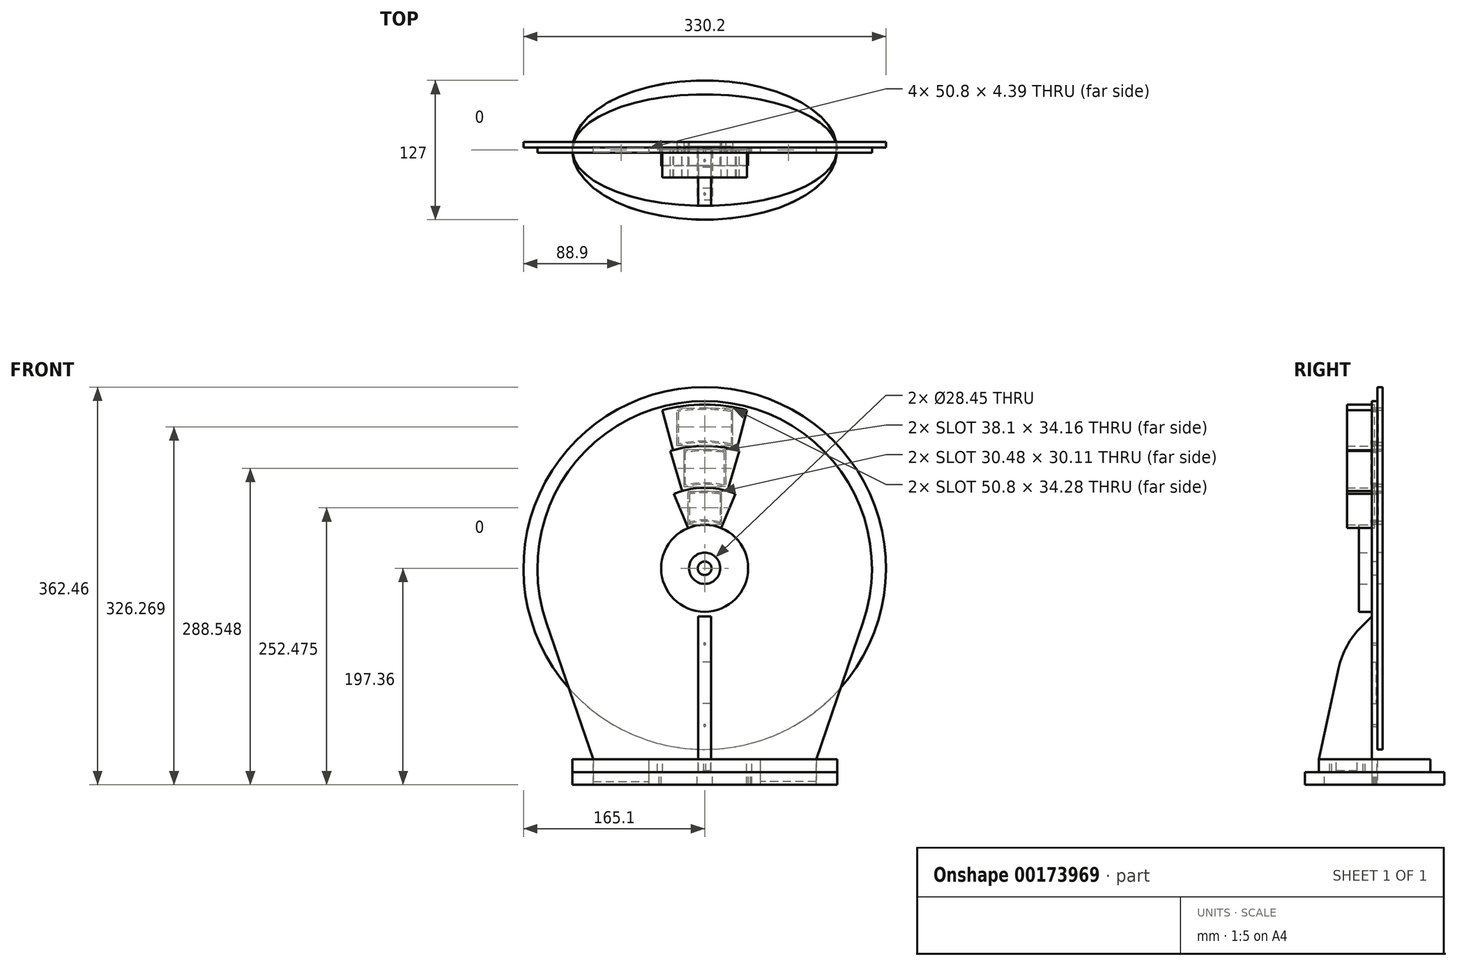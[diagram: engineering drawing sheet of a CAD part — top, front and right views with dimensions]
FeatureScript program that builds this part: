
annotation { "Feature Type Name" : "Feature", "Feature Type Description" : "" }
export const myFeature = defineFeature(function(context is Context, id is Id, definition is map)
    precondition{}
    {
        {
            var Q0;
            Q0=qCreatedBy(makeId("Front.planeOp"),FACE);
            var sketch = newSketch(context, id + "F0", { "sketchPlane" : qUnion([Q0])});
            skArc(sketch, "E0", {"start": v(144.21, 147.57) * mm, "mid": v(0, 349.25) * mm, "end": v(-144.21, 147.57) * mm});
            skLineSegment(sketch, "E1", {"start": v(0, 0) * mm, "end": v(0, 196.85) * mm, "construction": true});
            skLineSegment(sketch, "E2", {"start": v(-101.6, 22.86) * mm, "end": v(0, 22.86) * mm, "construction": true});
            skLineSegment(sketch, "E3", {"start": v(-101.6, 22.86) * mm, "end": v(-144.21, 147.57) * mm});
            skLineSegment(sketch, "E4.MirrorCS", {"start": v(101.6, 22.86) * mm, "end": v(0, 22.86) * mm, "construction": true});
            skLineSegment(sketch, "E5.MirrorCS", {"start": v(101.6, 22.86) * mm, "end": v(144.21, 147.57) * mm});
            skLineSegment(sketch, "E6", {"start": v(-101.6, 22.86) * mm, "end": v(-101.6, 2.54) * mm});
            skLineSegment(sketch, "E7", {"start": v(-101.6, 2.54) * mm, "end": v(-50.8, 2.54) * mm});
            skLineSegment(sketch, "E8", {"start": v(-50.8, 2.54) * mm, "end": v(-50.8, 22.86) * mm});
            skLineSegment(sketch, "E9", {"start": v(-50.8, 22.86) * mm, "end": v(0, 22.86) * mm});
            skLineSegment(sketch, "E10.MirrorCS", {"start": v(50.8, 2.54) * mm, "end": v(50.8, 22.86) * mm});
            skLineSegment(sketch, "E11.MirrorCS", {"start": v(50.8, 22.86) * mm, "end": v(0, 22.86) * mm});
            skLineSegment(sketch, "E12.MirrorCS", {"start": v(101.6, 22.86) * mm, "end": v(101.6, 2.54) * mm});
            skLineSegment(sketch, "E13.MirrorCS", {"start": v(101.6, 2.54) * mm, "end": v(50.8, 2.54) * mm});
            skCircle(sketch, "E14", {"center": v(0, 196.85) * mm, "radius": 6.22 * mm});
            skCircle(sketch, "E15", {"center": v(0, 196.85) * mm, "radius": 165.1 * mm, "construction": true});
            skCircle(sketch, "E16", {"center": v(0, 196.85) * mm, "radius": 39.69 * mm, "construction": true});
            skLineSegment(sketch, "E17.bottom", {"start": v(5.71, 73.66) * mm, "end": v(-5.72, 73.66) * mm});
            skLineSegment(sketch, "E17.top", {"start": v(5.71, 111.5) * mm, "end": v(-5.72, 111.5) * mm});
            skLineSegment(sketch, "E17.left", {"start": v(5.71, 73.66) * mm, "end": v(5.71, 111.5) * mm});
            skLineSegment(sketch, "E17.right", {"start": v(-5.72, 73.66) * mm, "end": v(-5.72, 111.5) * mm});
            skPoint(sketch, "E17.middle", {"position": v(0, 92.58) * mm});
            skCircle(sketch, "E18", {"center": v(0, 53.66) * mm, "radius": 0.95 * mm});
            skCircle(sketch, "E19", {"center": v(0, 128.02) * mm, "radius": 0.95 * mm});
            skSolve(sketch);
        }
        {
            var Q0;
            Q0=makeQuery(id+"F0.imprint","IMPRINT",FACE,{"disambiguationData":[TD([[makeQuery(id+"F0.imprint","IMPRINT",EDGE,{"derivedFrom":sQuery(id+"F0.wireOp",EDGE,"E0")}),1.0]])]});
            extrude(context, id + "F1", {"entities" : qUnion([Q0]), "endBound" : BoundingType.SYMMETRIC, "depth" : 4.9 * mm});
        }
        {
            var Q0;
            Q0=makeQuery(id+"F1.opExtrude","CAP_FACE",FACE,{"disambiguationData":[OSD([sQuery(id+"F0.wireOp",EDGE,"E0"),sQuery(id+"F0.wireOp",EDGE,"E3"),sQuery(id+"F0.wireOp",EDGE,"E5.MirrorCS"),sQuery(id+"F0.wireOp",EDGE,"E6"),sQuery(id+"F0.wireOp",EDGE,"E7"),sQuery(id+"F0.wireOp",EDGE,"E8"),sQuery(id+"F0.wireOp",EDGE,"E9"),sQuery(id+"F0.wireOp",EDGE,"E10.MirrorCS"),sQuery(id+"F0.wireOp",EDGE,"E11.MirrorCS"),sQuery(id+"F0.wireOp",EDGE,"E12.MirrorCS"),sQuery(id+"F0.wireOp",EDGE,"E13.MirrorCS"),sQuery(id+"F0.wireOp",EDGE,"E14")])],"isStart":false});
            var sketch = newSketch(context, id + "F2", { "sketchPlane" : qUnion([Q0])});
            skCircle(sketch, "E20", {"center": v(0, 196.85) * mm, "radius": 14.22 * mm});
            skCircle(sketch, "E21", {"center": v(0, 196.85) * mm, "radius": 39.62 * mm});
            skSolve(sketch);
        }
        {
            var Q0;
            Q0 = qSketchRegion(id + "F2", true);
            extrude(context, id + "F3", {"entities" : qUnion([Q0]), "depth" : 11.68 * mm});
        }
        {
            var Q0;
            Q0=makeQuery(id+"F1.opExtrude","CAP_FACE",FACE,{"disambiguationData":[OSD([sQuery(id+"F0.wireOp",EDGE,"E0"),sQuery(id+"F0.wireOp",EDGE,"E3"),sQuery(id+"F0.wireOp",EDGE,"E5.MirrorCS"),sQuery(id+"F0.wireOp",EDGE,"E6"),sQuery(id+"F0.wireOp",EDGE,"E7"),sQuery(id+"F0.wireOp",EDGE,"E8"),sQuery(id+"F0.wireOp",EDGE,"E9"),sQuery(id+"F0.wireOp",EDGE,"E10.MirrorCS"),sQuery(id+"F0.wireOp",EDGE,"E11.MirrorCS"),sQuery(id+"F0.wireOp",EDGE,"E12.MirrorCS"),sQuery(id+"F0.wireOp",EDGE,"E13.MirrorCS"),sQuery(id+"F0.wireOp",EDGE,"E14")])],"isStart":true});
            var sketch = newSketch(context, id + "F4", { "sketchPlane" : qUnion([Q0])});
            skCircle(sketch, "E22", {"center": v(0, 196.85) * mm, "radius": 14.22 * mm});
            skCircle(sketch, "E23", {"center": v(0, 196.85) * mm, "radius": 165.1 * mm});
            skSolve(sketch);
        }
        {
            var Q0;
            Q0=makeQuery(id+"F4.imprint","IMPRINT",FACE,{"disambiguationData":[TD([[makeQuery(id+"F4.imprint","IMPRINT",EDGE,{"derivedFrom":sQuery(id+"F4.wireOp",EDGE,"E22")}),-1.0]])]});
            var Q1;
            Q1=makeQuery(id+"F4.imprint","IMPRINT",FACE,{"disambiguationData":[TD([[makeQuery(id+"F4.imprint","IMPRINT",EDGE,{"derivedFrom":makeQuery(id+"F1.opExtrude","CAP_EDGE",EDGE,{"disambiguationData":[OSD([sQuery(id+"F0.wireOp",EDGE,"E17.bottom")])],"isStart":true})}),1.0]])]});
            var Q2;
            {var subQ5=makeQuery(id+"F1.opExtrude","CAP_EDGE",EDGE,{"disambiguationData":[OSD([sQuery(id+"F0.wireOp",EDGE,"E0")])],"isStart":true});Q2=makeQuery(id+"F4.imprint","IMPRINT",FACE,{"disambiguationData":[TD([[makeQuery(id+"F4.imprint","IMPRINT",EDGE,{"derivedFrom":subQ5}),1.0]])]});}
            var Q3;
            Q3=makeQuery(id+"F4.imprint","IMPRINT",FACE,{"disambiguationData":[TD([[makeQuery(id+"F4.imprint","IMPRINT",EDGE,{"derivedFrom":makeQuery(id+"F1.opExtrude","CAP_EDGE",EDGE,{"disambiguationData":[OSD([sQuery(id+"F0.wireOp",EDGE,"E19")])],"isStart":true})}),-1.0]])]});
            var Q4;
            Q4=makeQuery(id+"F4.imprint","IMPRINT",FACE,{"disambiguationData":[TD([[makeQuery(id+"F4.imprint","IMPRINT",EDGE,{"derivedFrom":makeQuery(id+"F1.opExtrude","CAP_EDGE",EDGE,{"disambiguationData":[OSD([sQuery(id+"F0.wireOp",EDGE,"E18")])],"isStart":true})}),-1.0]])]});
            extrude(context, id + "F5", {"entities" : qUnion([Q0, Q1, Q2, Q3, Q4]), "depth" : 4.9 * mm});
        }
        {
            var Q0;
            Q0=qCreatedBy(makeId("Front.planeOp"),FACE);
            var sketch = newSketch(context, id + "F6", { "sketchPlane" : qUnion([Q0])});
            skArc(sketch, "E24.0.1", {"start": v(144.21, 147.57) * mm, "mid": v(0, 349.25) * mm, "end": v(-144.21, 147.57) * mm, "construction": true});
            skCircle(sketch, "E25.0", {"center": v(0, 196.85) * mm, "radius": 165.1 * mm, "construction": true});
            skCircle(sketch, "E26.0", {"center": v(0, 196.85) * mm, "radius": 39.69 * mm, "construction": true});
            skCircle(sketch, "E27", {"center": v(0, 196.85) * mm, "radius": 152.4 * mm, "construction": true});
            skCircle(sketch, "E28", {"center": v(0, 196.85) * mm, "radius": 146.05 * mm});
            skCircle(sketch, "E29", {"center": v(0, 196.85) * mm, "radius": 114.62 * mm});
            skCircle(sketch, "E30", {"center": v(0, 196.85) * mm, "radius": 108.27 * mm});
            skCircle(sketch, "E31", {"center": v(0, 196.85) * mm, "radius": 76.52 * mm});
            skCircle(sketch, "E32", {"center": v(0, 196.85) * mm, "radius": 70.17 * mm});
            skCircle(sketch, "E33", {"center": v(0, 196.85) * mm, "radius": 42.86 * mm});
            skLineSegment(sketch, "E34", {"start": v(0, 196.85) * mm, "end": v(0, 267.02) * mm, "construction": true});
            skLineSegment(sketch, "E35", {"start": v(-15.24, 265.34) * mm, "end": v(-15.24, 236.91) * mm});
            skLineSegment(sketch, "E36.MirrorCS", {"start": v(15.24, 265.34) * mm, "end": v(15.24, 236.91) * mm});
            skLineSegment(sketch, "E37", {"start": v(-19.05, 270.96) * mm, "end": v(-19.05, 303.43) * mm});
            skLineSegment(sketch, "E38.MirrorCS", {"start": v(19.05, 270.96) * mm, "end": v(19.05, 303.43) * mm});
            skLineSegment(sketch, "E39", {"start": v(-25.4, 340.67) * mm, "end": v(-25.4, 308.62) * mm});
            skLineSegment(sketch, "E40.MirrorCS", {"start": v(25.4, 340.67) * mm, "end": v(25.4, 308.62) * mm});
            skSolve(sketch);
        }
        {
            var Q0;
            {var subQ0=sQuery(id+"F6.wireOp",EDGE,"E39");Q0=makeQuery(id+"F6.imprint","IMPRINT",FACE,{"disambiguationData":[TD([[makeQuery(id+"F6.imprint","IMPRINT",EDGE,{"derivedFrom":subQ0}),1.0]])]});}
            var Q1;
            {var subQ0=sQuery(id+"F6.wireOp",EDGE,"E37");Q1=makeQuery(id+"F6.imprint","IMPRINT",FACE,{"disambiguationData":[TD([[makeQuery(id+"F6.imprint","IMPRINT",EDGE,{"derivedFrom":subQ0}),-1.0]])]});}
            var Q2;
            {var subQ0=sQuery(id+"F6.wireOp",EDGE,"E35");Q2=makeQuery(id+"F6.imprint","IMPRINT",FACE,{"disambiguationData":[TD([[makeQuery(id+"F6.imprint","IMPRINT",EDGE,{"derivedFrom":subQ0}),1.0]])]});}
            extrude(context, id + "F7", {"entities" : qUnion([Q0, Q1, Q2]), "operationType" : NewBodyOperationType.REMOVE, "endBound" : BoundingType.THROUGH_ALL, "oppositeDirection" : true, "depth" : 25.4 * mm, "hasSecondDirection" : true, "secondDirectionBound" : SecondDirectionBoundingType.THROUGH_ALL, "secondDirectionOppositeDirection" : false, "secondDirectionDepth" : 25.4 * mm});
        }
        {
            var Q0;
            Q0=qCreatedBy(makeId("Front.planeOp"),FACE);
            var sketch = newSketch(context, id + "F8", { "sketchPlane" : qUnion([Q0])});
            skArc(sketch, "E41.4", {"start": v(15.24, 265.34) * mm, "mid": v(0, 267.02) * mm, "end": v(-15.24, 265.34) * mm, "construction": true});
            skLineSegment(sketch, "E41.5", {"start": v(-15.24, 265.34) * mm, "end": v(-15.24, 236.91) * mm, "construction": true});
            skArc(sketch, "E41.6", {"start": v(15.24, 236.91) * mm, "mid": v(0, 239.71) * mm, "end": v(-15.24, 236.91) * mm, "construction": true});
            skLineSegment(sketch, "E41.7", {"start": v(15.24, 265.34) * mm, "end": v(15.24, 236.91) * mm, "construction": true});
            skArc(sketch, "E42.0", {"start": v(13.97, 238.71) * mm, "mid": v(0, 240.98) * mm, "end": v(-13.97, 238.71) * mm});
            skLineSegment(sketch, "E42.1", {"start": v(13.97, 264.32) * mm, "end": v(13.97, 238.71) * mm});
            skArc(sketch, "E42.2", {"start": v(13.97, 264.32) * mm, "mid": v(0, 265.75) * mm, "end": v(-13.97, 264.32) * mm});
            skLineSegment(sketch, "E42.3", {"start": v(-13.97, 264.32) * mm, "end": v(-13.97, 238.71) * mm});
            skLineSegment(sketch, "E43.0", {"start": v(-25.4, 340.67) * mm, "end": v(-25.4, 308.62) * mm, "construction": true});
            skArc(sketch, "E43.1", {"start": v(25.4, 340.67) * mm, "mid": v(0, 342.9) * mm, "end": v(-25.4, 340.67) * mm, "construction": true});
            skLineSegment(sketch, "E43.2", {"start": v(25.4, 340.67) * mm, "end": v(25.4, 308.62) * mm, "construction": true});
            skArc(sketch, "E43.3", {"start": v(25.4, 308.62) * mm, "mid": v(0, 311.47) * mm, "end": v(-25.4, 308.62) * mm, "construction": true});
            skArc(sketch, "E44.0", {"start": v(19.05, 303.43) * mm, "mid": v(0, 305.12) * mm, "end": v(-19.05, 303.43) * mm, "construction": true});
            skLineSegment(sketch, "E44.1", {"start": v(-19.05, 270.96) * mm, "end": v(-19.05, 303.43) * mm, "construction": true});
            skArc(sketch, "E44.2", {"start": v(19.05, 270.96) * mm, "mid": v(0, 273.37) * mm, "end": v(-19.05, 270.96) * mm, "construction": true});
            skLineSegment(sketch, "E44.3", {"start": v(19.05, 270.96) * mm, "end": v(19.05, 303.43) * mm, "construction": true});
            skArc(sketch, "E45.0", {"start": v(24.13, 310.2) * mm, "mid": v(0, 312.74) * mm, "end": v(-24.13, 310.2) * mm});
            skLineSegment(sketch, "E45.1", {"start": v(24.13, 339.6) * mm, "end": v(24.13, 310.2) * mm});
            skArc(sketch, "E45.2", {"start": v(24.13, 339.6) * mm, "mid": v(0, 341.63) * mm, "end": v(-24.13, 339.6) * mm});
            skLineSegment(sketch, "E45.3", {"start": v(-24.13, 339.6) * mm, "end": v(-24.13, 310.2) * mm});
            skArc(sketch, "E46.0", {"start": v(17.78, 302.36) * mm, "mid": v(0, 303.85) * mm, "end": v(-17.78, 302.36) * mm});
            skLineSegment(sketch, "E46.1", {"start": v(17.78, 272.58) * mm, "end": v(17.78, 302.36) * mm});
            skArc(sketch, "E46.2", {"start": v(17.78, 272.58) * mm, "mid": v(0, 274.64) * mm, "end": v(-17.78, 272.58) * mm});
            skLineSegment(sketch, "E46.3", {"start": v(-17.78, 272.58) * mm, "end": v(-17.78, 302.36) * mm});
            skSolve(sketch);
        }
        {
            var Q0;
            Q0 = qSketchRegion(id + "F8", true);
            extrude(context, id + "F9", {"entities" : qUnion([Q0]), "endBound" : BoundingType.SYMMETRIC, "depth" : 6.35 * mm});
        }
        {
            var Q0;
            Q0=makeQuery(id+"F1.opExtrude","SWEPT_FACE",FACE,{"disambiguationData":[OSD([sQuery(id+"F0.wireOp",EDGE,"E9"),sQuery(id+"F0.wireOp",EDGE,"E11.MirrorCS")])]});
            var sketch = newSketch(context, id + "F10", { "sketchPlane" : qUnion([Q0])});
            skLineSegment(sketch, "E47.0.0", {"start": v(-101.6, -2.45) * mm, "end": v(-50.8, -2.45) * mm});
            skLineSegment(sketch, "E47.0.1", {"start": v(-50.8, -2.45) * mm, "end": v(-50.8, 2.45) * mm});
            skLineSegment(sketch, "E47.0.2", {"start": v(-50.8, 2.45) * mm, "end": v(-101.6, 2.45) * mm});
            skLineSegment(sketch, "E47.0.3", {"start": v(-101.6, 2.45) * mm, "end": v(-101.6, -2.45) * mm});
            skLineSegment(sketch, "E48.0.0", {"start": v(50.8, -2.45) * mm, "end": v(101.6, -2.45) * mm});
            skLineSegment(sketch, "E48.0.1", {"start": v(101.6, -2.45) * mm, "end": v(101.6, 2.45) * mm});
            skLineSegment(sketch, "E48.0.2", {"start": v(101.6, 2.45) * mm, "end": v(50.8, 2.45) * mm});
            skLineSegment(sketch, "E48.0.3", {"start": v(50.8, 2.45) * mm, "end": v(50.8, -2.45) * mm});
            skEllipse(sketch, "E49", {"center": v(0, 0) * mm, "majorRadius": 50.8 * mm, "minorRadius": 120.65 * mm, "majorAxis": v(0, 1)});
            skLineSegment(sketch, "E50", {"start": v(0, 0) * mm, "end": v(0, 50.8) * mm, "construction": true});
            skLineSegment(sketch, "E51", {"start": v(0, 0) * mm, "end": v(-120.65, 0) * mm, "construction": true});
            skLineSegment(sketch, "E52.bottom", {"start": v(5.59, 15.88) * mm, "end": v(-5.59, 15.88) * mm});
            skLineSegment(sketch, "E52.top", {"start": v(5.59, 34.93) * mm, "end": v(-5.59, 34.93) * mm});
            skLineSegment(sketch, "E52.left", {"start": v(5.59, 15.87) * mm, "end": v(5.59, 34.92) * mm});
            skLineSegment(sketch, "E52.right", {"start": v(-5.59, 15.88) * mm, "end": v(-5.59, 34.93) * mm});
            skPoint(sketch, "E52.middle", {"position": v(0, 25.4) * mm});
            skCircle(sketch, "E53", {"center": v(-40.64, 0) * mm, "radius": 2.29 * mm});
            skCircle(sketch, "E54.MirrorC", {"center": v(40.64, 0) * mm, "radius": 2.29 * mm});
            skCircle(sketch, "E55", {"center": v(0, 9.53) * mm, "radius": 0.95 * mm});
            skCircle(sketch, "E56", {"center": v(0, 40) * mm, "radius": 0.95 * mm});
            skLineSegment(sketch, "E57", {"start": v(-101.6, -2.2) * mm, "end": v(-50.8, -2.2) * mm});
            skLineSegment(sketch, "E58.MirrorCS", {"start": v(-101.6, 2.2) * mm, "end": v(-50.8, 2.2) * mm});
            skLineSegment(sketch, "E59.MirrorCS", {"start": v(101.6, 2.2) * mm, "end": v(50.8, 2.2) * mm});
            skLineSegment(sketch, "E60.MirrorCS", {"start": v(101.6, -2.2) * mm, "end": v(50.8, -2.2) * mm});
            skSolve(sketch);
        }
        {
            var Q0;
            Q0=makeQuery(id+"F10.imprint","IMPRINT",FACE,{"disambiguationData":[TD([[makeQuery(id+"F10.imprint","IMPRINT",EDGE,{"derivedFrom":sQuery(id+"F10.wireOp",EDGE,"E47.0.0")}),-1.0]])]});
            var Q1;
            Q1=makeQuery(id+"F10.imprint","IMPRINT",FACE,{"disambiguationData":[TD([[makeQuery(id+"F10.imprint","IMPRINT",EDGE,{"derivedFrom":sQuery(id+"F10.wireOp",EDGE,"E47.0.1")}),1.0]])]});
            var Q2;
            {var subQ0=sQuery(id+"F10.wireOp",EDGE,"E47.0.0");Q2=makeQuery(id+"F10.imprint","IMPRINT",FACE,{"disambiguationData":[TD([[makeQuery(id+"F10.imprint","IMPRINT",EDGE,{"derivedFrom":subQ0}),1.0]])]});}
            var Q3;
            {var subQ0=sQuery(id+"F10.wireOp",EDGE,"E47.0.2");Q3=makeQuery(id+"F10.imprint","IMPRINT",FACE,{"disambiguationData":[TD([[makeQuery(id+"F10.imprint","IMPRINT",EDGE,{"derivedFrom":subQ0}),1.0]])]});}
            var Q4;
            {var subQ0=sQuery(id+"F10.wireOp",EDGE,"E48.0.2");Q4=makeQuery(id+"F10.imprint","IMPRINT",FACE,{"disambiguationData":[TD([[makeQuery(id+"F10.imprint","IMPRINT",EDGE,{"derivedFrom":subQ0}),1.0]])]});}
            var Q5;
            {var subQ0=sQuery(id+"F10.wireOp",EDGE,"E48.0.0");Q5=makeQuery(id+"F10.imprint","IMPRINT",FACE,{"disambiguationData":[TD([[makeQuery(id+"F10.imprint","IMPRINT",EDGE,{"derivedFrom":subQ0}),1.0]])]});}
            extrude(context, id + "F11", {"entities" : qUnion([Q0, Q1, Q2, Q3, Q4, Q5]), "depth" : 11.68 * mm});
        }
        {
            var Q0;
            Q0=makeQuery(id+"F11.opExtrude","CAP_FACE",FACE,{"disambiguationData":[OSD([sQuery(id+"F10.wireOp",EDGE,"E47.0.0"),sQuery(id+"F10.wireOp",EDGE,"E47.0.1"),sQuery(id+"F10.wireOp",EDGE,"E47.0.2"),sQuery(id+"F10.wireOp",EDGE,"E47.0.3"),sQuery(id+"F10.wireOp",EDGE,"E48.0.0"),sQuery(id+"F10.wireOp",EDGE,"E48.0.1"),sQuery(id+"F10.wireOp",EDGE,"E48.0.2"),sQuery(id+"F10.wireOp",EDGE,"E48.0.3"),sQuery(id+"F10.wireOp",EDGE,"E49"),sQuery(id+"F10.wireOp",EDGE,"E52.bottom"),sQuery(id+"F10.wireOp",EDGE,"E52.top"),sQuery(id+"F10.wireOp",EDGE,"E52.left"),sQuery(id+"F10.wireOp",EDGE,"E52.right")])],"isStart":false});
            var sketch = newSketch(context, id + "F12", { "sketchPlane" : qUnion([Q0])});
            skEllipse(sketch, "E61", {"center": v(0, 0) * mm, "majorRadius": 63.5 * mm, "minorRadius": 120.65 * mm, "majorAxis": v(0, 1)});
            skLineSegment(sketch, "E62", {"start": v(0, 0) * mm, "end": v(0, 63.5) * mm, "construction": true});
            skLineSegment(sketch, "E63.bottom", {"start": v(6.98, 0) * mm, "end": v(-6.99, 0) * mm});
            skLineSegment(sketch, "E63.top", {"start": v(6.99, 45.72) * mm, "end": v(-6.99, 45.72) * mm});
            skLineSegment(sketch, "E63.left", {"start": v(6.98, 0) * mm, "end": v(6.98, 45.72) * mm});
            skLineSegment(sketch, "E63.right", {"start": v(-6.99, 0) * mm, "end": v(-6.99, 45.72) * mm});
            skPoint(sketch, "E63.middle", {"position": v(0, 22.86) * mm});
            skCircle(sketch, "E64.0", {"center": v(-40.64, 0) * mm, "radius": 2.29 * mm, "construction": true});
            skCircle(sketch, "E65", {"center": v(-40.64, 0) * mm, "radius": 0.95 * mm});
            skCircle(sketch, "E66.MirrorC", {"center": v(40.64, 0) * mm, "radius": 0.95 * mm});
            skLineSegment(sketch, "E67.0", {"start": v(-101.6, -2.2) * mm, "end": v(-50.8, -2.2) * mm});
            skLineSegment(sketch, "E67.1", {"start": v(-50.8, 2.2) * mm, "end": v(-50.8, -2.2) * mm});
            skLineSegment(sketch, "E67.2", {"start": v(-101.6, 2.2) * mm, "end": v(-50.8, 2.2) * mm});
            skLineSegment(sketch, "E67.3", {"start": v(-101.6, 2.2) * mm, "end": v(-101.6, -2.2) * mm});
            skLineSegment(sketch, "E68.0", {"start": v(101.6, -2.2) * mm, "end": v(101.6, 2.2) * mm});
            skLineSegment(sketch, "E68.1", {"start": v(101.6, 2.2) * mm, "end": v(50.8, 2.2) * mm});
            skLineSegment(sketch, "E68.2", {"start": v(50.8, 2.2) * mm, "end": v(50.8, -2.2) * mm});
            skLineSegment(sketch, "E68.3", {"start": v(101.6, -2.2) * mm, "end": v(50.8, -2.2) * mm});
            skSolve(sketch);
        }
        {
            var Q0;
            {var subQ0=sQuery(id+"F12.wireOp",EDGE,"E61");var subQ1=makeQuery(id+"F11.opExtrude","CAP_EDGE",EDGE,{"disambiguationData":[OSD([sQuery(id+"F10.wireOp",EDGE,"E49")])],"isStart":false});var subQ2=makeQuery(id+"F12.imprint","INTERSECT",VERTEX,{"disambiguationData":[OD(0.0)],"derivedFrom":[subQ1,subQ0]});Q0=makeQuery(id+"F12.imprint","IMPRINT",FACE,{"disambiguationData":[TD([[makeQuery(id+"F12.imprint","IMPRINT",EDGE,{"disambiguationData":[TD([[subQ2,1.0]])],"derivedFrom":subQ0}),1.0]])]});}
            var Q1;
            Q1=makeQuery(id+"F12.imprint","IMPRINT",FACE,{"disambiguationData":[TD([[makeQuery(id+"F12.imprint","IMPRINT",EDGE,{"derivedFrom":sQuery(id+"F12.wireOp",EDGE,"c6ddadf6-0816-4154-b7ff-1b20ffb77494.0.0")}),-1.0]])]});
            var Q2;
            {var subQ3=makeQuery(id+"F11.opExtrude","CAP_EDGE",EDGE,{"disambiguationData":[OSD([sQuery(id+"F10.wireOp",EDGE,"E49")])],"isStart":false});var subQ6=sQuery(id+"F12.wireOp",EDGE,"E61");var subQ7=makeQuery(id+"F12.imprint","INTERSECT",VERTEX,{"disambiguationData":[OD(0.0)],"derivedFrom":[subQ3,subQ6]});Q2=makeQuery(id+"F12.imprint","IMPRINT",FACE,{"disambiguationData":[TD([[makeQuery(id+"F12.imprint","IMPRINT",EDGE,{"disambiguationData":[TD([[subQ7,-1.0]])],"derivedFrom":subQ6}),1.0]])]});}
            var Q3;
            Q3=makeQuery(id+"F12.imprint","IMPRINT",FACE,{"disambiguationData":[TD([[makeQuery(id+"F12.imprint","IMPRINT",EDGE,{"derivedFrom":sQuery(id+"F12.wireOp",EDGE,"E65")}),-1.0]])]});
            var Q4;
            Q4=makeQuery(id+"F12.imprint","IMPRINT",FACE,{"disambiguationData":[TD([[makeQuery(id+"F12.imprint","IMPRINT",EDGE,{"derivedFrom":sQuery(id+"F12.wireOp",EDGE,"E66.MirrorC")}),1.0]])]});
            var Q5;
            Q5=makeQuery(id+"F12.imprint","IMPRINT",FACE,{"disambiguationData":[TD([[makeQuery(id+"F12.imprint","IMPRINT",EDGE,{"derivedFrom":sQuery(id+"F12.wireOp",EDGE,"E63.bottom")}),1.0]])]});
            extrude(context, id + "F13", {"entities" : qUnion([Q0, Q1, Q2, Q3, Q4, Q5]), "depth" : 11.68 * mm});
        }
        {
            var Q0;
            Q0=qCreatedBy(makeId("Right.planeOp"),FACE);
            var sketch = newSketch(context, id + "F14", { "sketchPlane" : qUnion([Q0])});
            skLineSegment(sketch, "E69.0", {"start": v(-2.45, 22.86) * mm, "end": v(-2.45, 147.57) * mm});
            skLineSegment(sketch, "E70.0", {"start": v(-50.8, 22.86) * mm, "end": v(-2.45, 22.86) * mm});
            skPoint(sketch, "E71.orphan", {"position": v(50.8, 22.86) * mm});
            skLineSegment(sketch, "E72.0", {"start": v(-2.45, 111.5) * mm, "end": v(1.18, 111.5) * mm});
            skLineSegment(sketch, "E73.0", {"start": v(-2.45, 73.66) * mm, "end": v(1.18, 73.66) * mm});
            skLineSegment(sketch, "E74.0", {"start": v(-15.88, 12.45) * mm, "end": v(-15.88, 22.86) * mm});
            skLineSegment(sketch, "E75.0", {"start": v(-34.92, 12.45) * mm, "end": v(-34.92, 22.86) * mm});
            skLineSegment(sketch, "E76", {"start": v(1.18, 111.5) * mm, "end": v(1.18, 73.66) * mm});
            skPoint(sketch, "E77.orphan", {"position": v(2.45, 111.5) * mm});
            skPoint(sketch, "E78.orphan", {"position": v(2.45, 73.66) * mm});
            skLineSegment(sketch, "E79", {"start": v(-15.88, 12.45) * mm, "end": v(-34.93, 12.45) * mm});
            skPoint(sketch, "E80.orphan", {"position": v(-15.88, 11.18) * mm});
            skPoint(sketch, "E81.orphan", {"position": v(-34.93, 11.18) * mm});
            skLineSegment(sketch, "E82", {"start": v(-2.45, 147.57) * mm, "end": v(-2.45, 153.03) * mm});
            skLineSegment(sketch, "E83", {"start": v(-2.45, 153.03) * mm, "end": v(-27.85, 127.64) * mm});
            skLineSegment(sketch, "E84", {"start": v(-27.85, 127.64) * mm, "end": v(-50.8, 22.86) * mm});
            skSolve(sketch);
        }
        {
            var Q0;
            {var subQ0=sQuery(id+"F14.wireOp",EDGE,"E72.0");Q0=makeQuery(id+"F14.imprint","IMPRINT",FACE,{"disambiguationData":[TD([[makeQuery(id+"F14.imprint","IMPRINT",EDGE,{"derivedFrom":subQ0}),-1.0]])]});}
            var Q1;
            {var subQ0=sQuery(id+"F14.wireOp",EDGE,"E74.0");Q1=makeQuery(id+"F14.imprint","IMPRINT",FACE,{"disambiguationData":[TD([[makeQuery(id+"F14.imprint","IMPRINT",EDGE,{"derivedFrom":subQ0}),1.0]])]});}
            var Q2;
            {var subQ0=sQuery(id+"F14.wireOp",EDGE,"342de165-3257-4ef9-9f4c-1146a8989881");Q2=makeQuery(id+"F14.imprint","IMPRINT",FACE,{"disambiguationData":[TD([[makeQuery(id+"F14.imprint","IMPRINT",EDGE,{"derivedFrom":subQ0}),-1.0]])]});}
            var Q3;
            {var subQ3=sQuery(id+"F14.wireOp",EDGE,"E82");Q3=makeQuery(id+"F14.imprint","IMPRINT",FACE,{"disambiguationData":[TD([[makeQuery(id+"F14.imprint","IMPRINT",EDGE,{"derivedFrom":subQ3}),1.0]])]});}
            extrude(context, id + "F15", {"entities" : qUnion([Q0, Q1, Q2, Q3]), "endBound" : BoundingType.SYMMETRIC, "depth" : 11.68 * mm});
        }
        {
            var Q0;
            Q0=makeQuery(id+"F15.opExtrude","SWEPT_EDGE",EDGE,{"disambiguationData":[OSD([sQuery(id+"F14.wireOp",EDGE,"E83"),sQuery(id+"F14.wireOp",EDGE,"E84")])]});
            fillet(context, id + "F16", {"entities" : qUnion([Q0]), "radius" : 75 * mm, "tangentPropagation" : true, "allowEdgeOverflow" : false});
        }
        {
            var Q0;
            Q0=qCreatedBy(makeId("Front.planeOp"),FACE);
            var sketch = newSketch(context, id + "F17", { "sketchPlane" : qUnion([Q0])});
            skCircle(sketch, "E85.0", {"center": v(0, 196.85) * mm, "radius": 6.22 * mm});
            skLineSegment(sketch, "E86", {"start": v(0, 196.85) * mm, "end": v(-28.07, 264.6) * mm});
            skCircle(sketch, "E87", {"center": v(0, 196.85) * mm, "radius": 73.34 * mm});
            skArc(sketch, "E88.0", {"start": v(19.05, 270.96) * mm, "mid": v(0, 273.37) * mm, "end": v(-19.05, 270.96) * mm});
            skArc(sketch, "E88.1", {"start": v(15.24, 265.34) * mm, "mid": v(0, 267.02) * mm, "end": v(-15.24, 265.34) * mm});
            skLineSegment(sketch, "E89", {"start": v(0, 267.02) * mm, "end": v(0, 270.2) * mm});
            skLineSegment(sketch, "E90", {"start": v(0, 270.2) * mm, "end": v(0, 273.37) * mm});
            skLineSegment(sketch, "E91.MirrorCS", {"start": v(0, 196.85) * mm, "end": v(28.07, 264.6) * mm});
            skCircle(sketch, "E92", {"center": v(0, 196.85) * mm, "radius": 39.69 * mm});
            skArc(sketch, "E93.0", {"start": v(15.24, 236.91) * mm, "mid": v(0, 239.71) * mm, "end": v(-15.24, 236.91) * mm});
            skLineSegment(sketch, "E94", {"start": v(0, 239.71) * mm, "end": v(0, 236.54) * mm});
            skCircle(sketch, "E95", {"center": v(0, 196.85) * mm, "radius": 111.44 * mm});
            skArc(sketch, "E96.0", {"start": v(25.4, 308.62) * mm, "mid": v(0, 311.47) * mm, "end": v(-25.4, 308.62) * mm});
            skArc(sketch, "E96.1", {"start": v(19.05, 303.43) * mm, "mid": v(0, 305.12) * mm, "end": v(-19.05, 303.43) * mm});
            skLineSegment(sketch, "E97", {"start": v(0, 311.47) * mm, "end": v(0, 308.3) * mm});
            skLineSegment(sketch, "E98", {"start": v(0, 308.3) * mm, "end": v(0, 305.12) * mm});
            skLineSegment(sketch, "E99", {"start": v(0, 196.85) * mm, "end": v(-31.42, 303.77) * mm});
            skLineSegment(sketch, "E100.MirrorCS", {"start": v(0, 196.85) * mm, "end": v(31.42, 303.77) * mm});
            skCircle(sketch, "E101", {"center": v(0, 196.85) * mm, "radius": 149.22 * mm});
            skArc(sketch, "E102.0", {"start": v(25.4, 340.67) * mm, "mid": v(0, 342.9) * mm, "end": v(-25.4, 340.67) * mm});
            skLineSegment(sketch, "E103", {"start": v(0, 342.9) * mm, "end": v(0, 346.07) * mm});
            skLineSegment(sketch, "E104", {"start": v(0, 196.85) * mm, "end": v(-38.62, 341) * mm});
            skLineSegment(sketch, "E105.MirrorCS", {"start": v(0, 196.85) * mm, "end": v(38.62, 341) * mm});
            skLineSegment(sketch, "E106.bottom", {"start": v(-38.62, 346.07) * mm, "end": v(38.62, 346.07) * mm});
            skLineSegment(sketch, "E106.top", {"start": v(-38.62, 304.52) * mm, "end": v(38.62, 304.52) * mm});
            skLineSegment(sketch, "E106.left", {"start": v(-38.62, 346.07) * mm, "end": v(-38.62, 304.52) * mm});
            skLineSegment(sketch, "E106.right", {"start": v(38.62, 346.07) * mm, "end": v(38.62, 304.52) * mm});
            skLineSegment(sketch, "E107.bottom", {"start": v(-31.42, 308.3) * mm, "end": v(31.42, 308.3) * mm});
            skLineSegment(sketch, "E107.top", {"start": v(-31.42, 267.18) * mm, "end": v(31.42, 267.18) * mm});
            skLineSegment(sketch, "E107.left", {"start": v(-31.42, 308.3) * mm, "end": v(-31.42, 267.18) * mm});
            skLineSegment(sketch, "E107.right", {"start": v(31.42, 308.3) * mm, "end": v(31.42, 267.18) * mm});
            skLineSegment(sketch, "E108.bottom", {"start": v(-28.07, 270.2) * mm, "end": v(28.07, 270.2) * mm});
            skLineSegment(sketch, "E108.top", {"start": v(-28.07, 233.46) * mm, "end": v(28.07, 233.46) * mm});
            skLineSegment(sketch, "E108.left", {"start": v(-28.07, 270.2) * mm, "end": v(-28.07, 233.46) * mm});
            skLineSegment(sketch, "E108.right", {"start": v(28.07, 270.2) * mm, "end": v(28.07, 233.46) * mm});
            skSolve(sketch);
        }
        {
            var Q0;
            {var subQ2=sQuery(id+"F17.wireOp",EDGE,"E92");var subQ6=sQuery(id+"F17.wireOp",EDGE,"E86");var subQ7=makeQuery(id+"F17.imprint","INTERSECT",VERTEX,{"derivedFrom":[subQ6,subQ2]});Q0=makeQuery(id+"F17.imprint","IMPRINT",FACE,{"disambiguationData":[TD([[makeQuery(id+"F17.imprint","IMPRINT",EDGE,{"disambiguationData":[TD([[subQ7,1.0]])],"derivedFrom":subQ2}),-1.0]])]});}
            var Q1;
            {var subQ0=sQuery(id+"F17.wireOp",EDGE,"E92");var subQ1=sQuery(id+"F17.wireOp",EDGE,"E91.MirrorCS");var subQ2=makeQuery(id+"F17.imprint","INTERSECT",VERTEX,{"derivedFrom":[subQ1,subQ0]});Q1=makeQuery(id+"F17.imprint","IMPRINT",FACE,{"disambiguationData":[TD([[makeQuery(id+"F17.imprint","IMPRINT",EDGE,{"disambiguationData":[TD([[subQ2,-1.0]])],"derivedFrom":subQ0}),-1.0]])]});}
            var Q2;
            {var subQ0=sQuery(id+"F17.wireOp",EDGE,"E104");var subQ1=sQuery(id+"F17.wireOp",EDGE,"E92");var subQ2=makeQuery(id+"F17.imprint","INTERSECT",VERTEX,{"derivedFrom":[subQ1,subQ0]});Q2=makeQuery(id+"F17.imprint","IMPRINT",FACE,{"disambiguationData":[TD([[makeQuery(id+"F17.imprint","IMPRINT",EDGE,{"disambiguationData":[TD([[subQ2,-1.0]])],"derivedFrom":subQ1}),-1.0]])]});}
            var Q3;
            {var subQ0=sQuery(id+"F17.wireOp",EDGE,"E94");Q3=makeQuery(id+"F17.imprint","IMPRINT",FACE,{"disambiguationData":[TD([[makeQuery(id+"F17.imprint","IMPRINT",EDGE,{"derivedFrom":subQ0}),-1.0]])]});}
            var Q4;
            {var subQ0=sQuery(id+"F17.wireOp",EDGE,"E94");Q4=makeQuery(id+"F17.imprint","IMPRINT",FACE,{"disambiguationData":[TD([[makeQuery(id+"F17.imprint","IMPRINT",EDGE,{"derivedFrom":subQ0}),1.0]])]});}
            var Q5;
            {var subQ0=sQuery(id+"F17.wireOp",EDGE,"E100.MirrorCS");var subQ1=sQuery(id+"F17.wireOp",EDGE,"E92");var subQ2=makeQuery(id+"F17.imprint","INTERSECT",VERTEX,{"derivedFrom":[subQ1,subQ0]});Q5=makeQuery(id+"F17.imprint","IMPRINT",FACE,{"disambiguationData":[TD([[makeQuery(id+"F17.imprint","IMPRINT",EDGE,{"disambiguationData":[TD([[subQ2,-1.0]])],"derivedFrom":subQ1}),-1.0]])]});}
            var Q6;
            {var subQ0=sQuery(id+"F17.wireOp",EDGE,"E100.MirrorCS");var subQ1=sQuery(id+"F17.wireOp",EDGE,"E93.0");var subQ2=makeQuery(id+"F17.imprint","INTERSECT",VERTEX,{"derivedFrom":[subQ1,subQ0]});Q6=makeQuery(id+"F17.imprint","IMPRINT",FACE,{"disambiguationData":[TD([[makeQuery(id+"F17.imprint","IMPRINT",EDGE,{"disambiguationData":[TD([[subQ2,-1.0]])],"derivedFrom":subQ1}),-1.0]])]});}
            var Q7;
            {var subQ1=sQuery(id+"F17.wireOp",EDGE,"E93.0");var subQ9=makeQuery(id+"F17.imprint","INTERSECT",VERTEX,{"derivedFrom":[subQ1,sQuery(id+"F17.wireOp",EDGE,"E94")]});Q7=makeQuery(id+"F17.imprint","IMPRINT",FACE,{"disambiguationData":[TD([[makeQuery(id+"F17.imprint","IMPRINT",EDGE,{"disambiguationData":[TD([[subQ9,1.0]])],"derivedFrom":subQ1}),-1.0]])]});}
            var Q8;
            {var subQ0=sQuery(id+"F17.wireOp",EDGE,"E99");var subQ1=sQuery(id+"F17.wireOp",EDGE,"E93.0");var subQ2=makeQuery(id+"F17.imprint","INTERSECT",VERTEX,{"derivedFrom":[subQ1,subQ0]});Q8=makeQuery(id+"F17.imprint","IMPRINT",FACE,{"disambiguationData":[TD([[makeQuery(id+"F17.imprint","IMPRINT",EDGE,{"disambiguationData":[TD([[subQ2,1.0]])],"derivedFrom":subQ1}),-1.0]])]});}
            var Q9;
            {var subQ1=sQuery(id+"F17.wireOp",EDGE,"E87");var subQ3=sQuery(id+"F17.wireOp",EDGE,"E104");var subQ4=makeQuery(id+"F17.imprint","INTERSECT",VERTEX,{"derivedFrom":[subQ1,subQ3]});Q9=makeQuery(id+"F17.imprint","IMPRINT",FACE,{"disambiguationData":[TD([[makeQuery(id+"F17.imprint","IMPRINT",EDGE,{"disambiguationData":[TD([[subQ4,1.0]])],"derivedFrom":subQ3}),-1.0]])]});}
            var Q10;
            {var subQ1=sQuery(id+"F17.wireOp",EDGE,"E87");var subQ3=sQuery(id+"F17.wireOp",EDGE,"E105.MirrorCS");var subQ4=makeQuery(id+"F17.imprint","INTERSECT",VERTEX,{"derivedFrom":[subQ1,subQ3]});Q10=makeQuery(id+"F17.imprint","IMPRINT",FACE,{"disambiguationData":[TD([[makeQuery(id+"F17.imprint","IMPRINT",EDGE,{"disambiguationData":[TD([[subQ4,1.0]])],"derivedFrom":subQ3}),1.0]])]});}
            var Q11;
            {var subQ0=sQuery(id+"F17.wireOp",EDGE,"E100.MirrorCS");var subQ1=sQuery(id+"F17.wireOp",EDGE,"E87");var subQ2=makeQuery(id+"F17.imprint","INTERSECT",VERTEX,{"derivedFrom":[subQ1,subQ0]});Q11=makeQuery(id+"F17.imprint","IMPRINT",FACE,{"disambiguationData":[TD([[makeQuery(id+"F17.imprint","IMPRINT",EDGE,{"disambiguationData":[TD([[subQ2,-1.0]])],"derivedFrom":subQ1}),1.0]])]});}
            var Q12;
            {var subQ0=sQuery(id+"F17.wireOp",EDGE,"E104");var subQ1=sQuery(id+"F17.wireOp",EDGE,"E87");var subQ2=makeQuery(id+"F17.imprint","INTERSECT",VERTEX,{"derivedFrom":[subQ1,subQ0]});Q12=makeQuery(id+"F17.imprint","IMPRINT",FACE,{"disambiguationData":[TD([[makeQuery(id+"F17.imprint","IMPRINT",EDGE,{"disambiguationData":[TD([[subQ2,-1.0]])],"derivedFrom":subQ1}),1.0]])]});}
            var Q13;
            {var subQ1=sQuery(id+"F17.wireOp",EDGE,"E101");var subQ9=makeQuery(id+"F17.imprint","INTERSECT",VERTEX,{"derivedFrom":[subQ1,sQuery(id+"F17.wireOp",EDGE,"E106.bottom")]});Q13=makeQuery(id+"F17.imprint","IMPRINT",FACE,{"disambiguationData":[TD([[makeQuery(id+"F17.imprint","IMPRINT",EDGE,{"disambiguationData":[TD([[subQ9,1.0]])],"derivedFrom":subQ1}),1.0]])]});}
            var Q14;
            {var subQ3=sQuery(id+"F17.wireOp",EDGE,"E106.top");var subQ5=sQuery(id+"F17.wireOp",EDGE,"E105.MirrorCS");var subQ6=makeQuery(id+"F17.imprint","INTERSECT",VERTEX,{"derivedFrom":[subQ5,subQ3]});Q14=makeQuery(id+"F17.imprint","IMPRINT",FACE,{"disambiguationData":[TD([[makeQuery(id+"F17.imprint","IMPRINT",EDGE,{"disambiguationData":[TD([[subQ6,-1.0]])],"derivedFrom":subQ5}),1.0]])]});}
            var Q15;
            {var subQ3=sQuery(id+"F17.wireOp",EDGE,"E106.top");var subQ5=sQuery(id+"F17.wireOp",EDGE,"E104");var subQ6=makeQuery(id+"F17.imprint","INTERSECT",VERTEX,{"derivedFrom":[subQ5,subQ3]});Q15=makeQuery(id+"F17.imprint","IMPRINT",FACE,{"disambiguationData":[TD([[makeQuery(id+"F17.imprint","IMPRINT",EDGE,{"disambiguationData":[TD([[subQ6,-1.0]])],"derivedFrom":subQ5}),-1.0]])]});}
            extrude(context, id + "F18", {"entities" : qUnion([Q0, Q1, Q2, Q3, Q4, Q5, Q6, Q7, Q8, Q9, Q10, Q11, Q12, Q13, Q14, Q15]), "depth" : 25 * mm});
        }
        {
            var Q0;
            {var subQ1=sQuery(id+"F17.wireOp",EDGE,"E95");var subQ3=sQuery(id+"F17.wireOp",EDGE,"E104");var subQ4=makeQuery(id+"F17.imprint","INTERSECT",VERTEX,{"derivedFrom":[subQ1,subQ3]});Q0=makeQuery(id+"F17.imprint","IMPRINT",FACE,{"disambiguationData":[TD([[makeQuery(id+"F17.imprint","IMPRINT",EDGE,{"disambiguationData":[TD([[subQ4,1.0]])],"derivedFrom":subQ3}),1.0]])]});}
            var Q1;
            {var subQ0=sQuery(id+"F17.wireOp",EDGE,"E104");var subQ1=sQuery(id+"F17.wireOp",EDGE,"E87");var subQ2=makeQuery(id+"F17.imprint","INTERSECT",VERTEX,{"derivedFrom":[subQ1,subQ0]});Q1=makeQuery(id+"F17.imprint","IMPRINT",FACE,{"disambiguationData":[TD([[makeQuery(id+"F17.imprint","IMPRINT",EDGE,{"disambiguationData":[TD([[subQ2,-1.0]])],"derivedFrom":subQ1}),-1.0]])]});}
            var Q2;
            {var subQ1=sQuery(id+"F17.wireOp",EDGE,"E87");var subQ3=sQuery(id+"F17.wireOp",EDGE,"E104");var subQ4=makeQuery(id+"F17.imprint","INTERSECT",VERTEX,{"derivedFrom":[subQ1,subQ3]});Q2=makeQuery(id+"F17.imprint","IMPRINT",FACE,{"disambiguationData":[TD([[makeQuery(id+"F17.imprint","IMPRINT",EDGE,{"disambiguationData":[TD([[subQ4,-1.0]])],"derivedFrom":subQ3}),-1.0]])]});}
            var Q3;
            {var subQ0=sQuery(id+"F17.wireOp",EDGE,"E105.MirrorCS");var subQ1=sQuery(id+"F17.wireOp",EDGE,"E95");var subQ2=makeQuery(id+"F17.imprint","INTERSECT",VERTEX,{"derivedFrom":[subQ1,subQ0]});Q3=makeQuery(id+"F17.imprint","IMPRINT",FACE,{"disambiguationData":[TD([[makeQuery(id+"F17.imprint","IMPRINT",EDGE,{"disambiguationData":[TD([[subQ2,-1.0]])],"derivedFrom":subQ1}),1.0]])]});}
            var Q4;
            {var subQ1=sQuery(id+"F17.wireOp",EDGE,"E87");var subQ3=sQuery(id+"F17.wireOp",EDGE,"E105.MirrorCS");var subQ4=makeQuery(id+"F17.imprint","INTERSECT",VERTEX,{"derivedFrom":[subQ1,subQ3]});Q4=makeQuery(id+"F17.imprint","IMPRINT",FACE,{"disambiguationData":[TD([[makeQuery(id+"F17.imprint","IMPRINT",EDGE,{"disambiguationData":[TD([[subQ4,-1.0]])],"derivedFrom":subQ3}),1.0]])]});}
            var Q5;
            {var subQ0=sQuery(id+"F17.wireOp",EDGE,"E100.MirrorCS");var subQ1=sQuery(id+"F17.wireOp",EDGE,"E87");var subQ2=makeQuery(id+"F17.imprint","INTERSECT",VERTEX,{"derivedFrom":[subQ1,subQ0]});Q5=makeQuery(id+"F17.imprint","IMPRINT",FACE,{"disambiguationData":[TD([[makeQuery(id+"F17.imprint","IMPRINT",EDGE,{"disambiguationData":[TD([[subQ2,-1.0]])],"derivedFrom":subQ1}),-1.0]])]});}
            var Q6;
            {var subQ1=sQuery(id+"F17.wireOp",EDGE,"E95");var subQ3=sQuery(id+"F17.wireOp",EDGE,"E105.MirrorCS");var subQ4=makeQuery(id+"F17.imprint","INTERSECT",VERTEX,{"derivedFrom":[subQ1,subQ3]});Q6=makeQuery(id+"F17.imprint","IMPRINT",FACE,{"disambiguationData":[TD([[makeQuery(id+"F17.imprint","IMPRINT",EDGE,{"disambiguationData":[TD([[subQ4,1.0]])],"derivedFrom":subQ3}),-1.0]])]});}
            var Q7;
            {var subQ0=sQuery(id+"F17.wireOp",EDGE,"E98");Q7=makeQuery(id+"F17.imprint","IMPRINT",FACE,{"disambiguationData":[TD([[makeQuery(id+"F17.imprint","IMPRINT",EDGE,{"derivedFrom":subQ0}),-1.0]])]});}
            var Q8;
            {var subQ0=sQuery(id+"F17.wireOp",EDGE,"E96.1");var subQ1=makeQuery(id+"F17.imprint","INTERSECT",VERTEX,{"derivedFrom":[subQ0,sQuery(id+"F17.wireOp",EDGE,"E98")]});Q8=makeQuery(id+"F17.imprint","IMPRINT",FACE,{"disambiguationData":[TD([[makeQuery(id+"F17.imprint","IMPRINT",EDGE,{"disambiguationData":[TD([[subQ1,1.0]])],"derivedFrom":subQ0}),1.0]])]});}
            var Q9;
            {var subQ0=sQuery(id+"F17.wireOp",EDGE,"E98");Q9=makeQuery(id+"F17.imprint","IMPRINT",FACE,{"disambiguationData":[TD([[makeQuery(id+"F17.imprint","IMPRINT",EDGE,{"derivedFrom":subQ0}),1.0]])]});}
            extrude(context, id + "F19", {"entities" : qUnion([Q0, Q1, Q2, Q3, Q4, Q5, Q6, Q7, Q8, Q9]), "depth" : 25 * mm});
        }
    });
